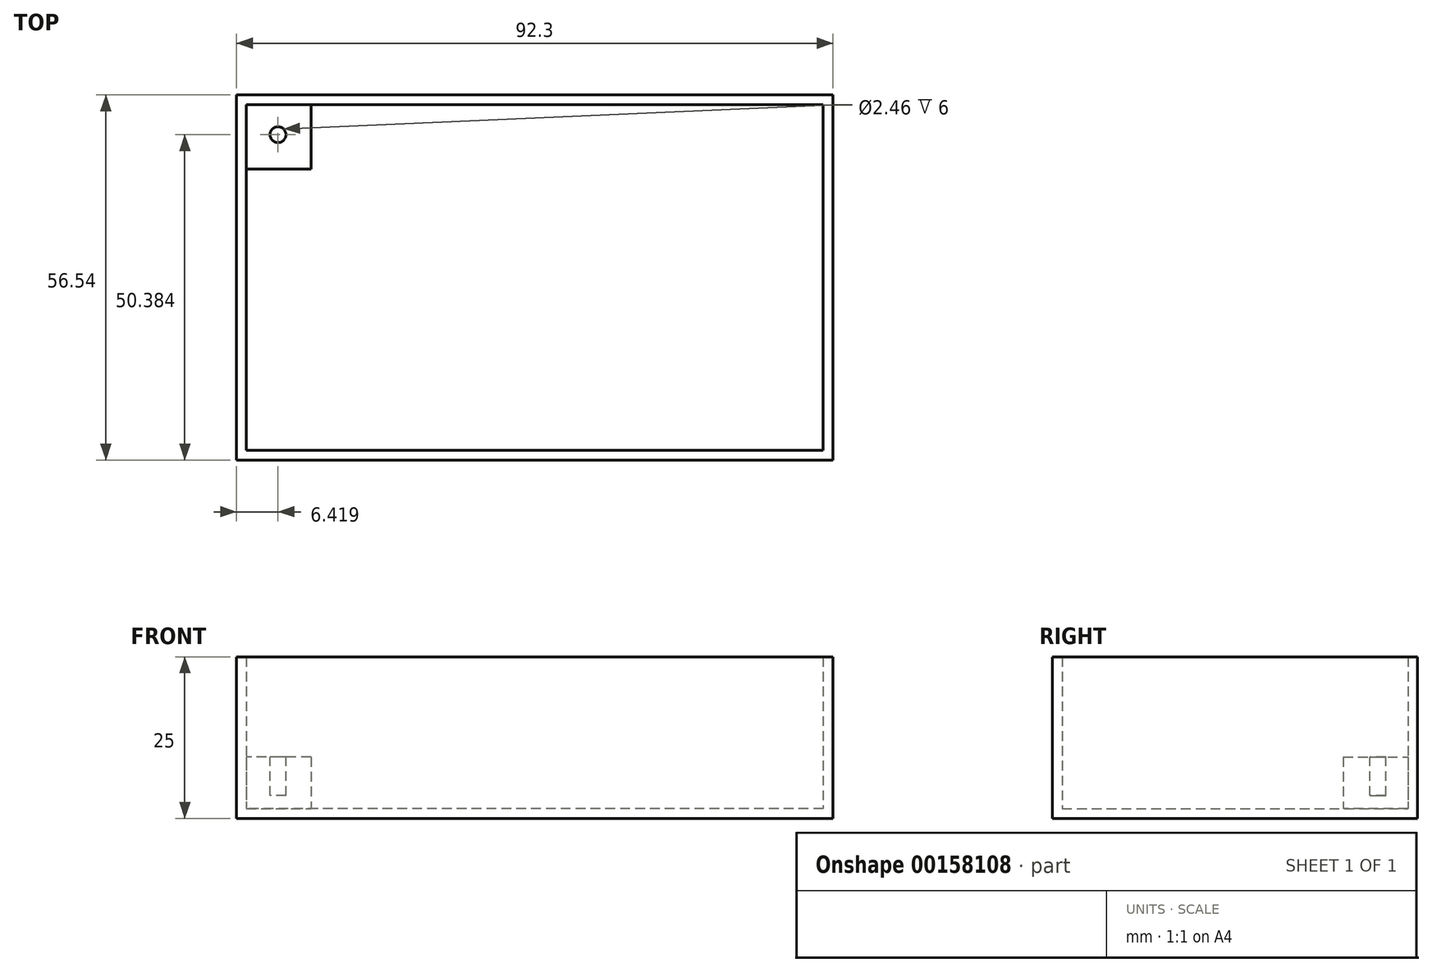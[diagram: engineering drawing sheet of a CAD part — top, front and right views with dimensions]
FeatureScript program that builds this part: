
annotation { "Feature Type Name" : "Feature", "Feature Type Description" : "" }
export const myFeature = defineFeature(function(context is Context, id is Id, definition is map)
    precondition{}
    {
        {
            var Q0;
            Q0=qCreatedBy(makeId("Top.planeOp"),FACE);
            var sketch = newSketch(context, id + "F0", { "sketchPlane" : qUnion([Q0])});
            skLineSegment(sketch, "E0.bottom", {"start": v(46.15, -28.27) * mm, "end": v(-46.15, -28.27) * mm});
            skLineSegment(sketch, "E0.top", {"start": v(46.15, 28.27) * mm, "end": v(-46.15, 28.27) * mm});
            skLineSegment(sketch, "E0.left", {"start": v(46.15, -28.27) * mm, "end": v(46.15, 28.27) * mm});
            skLineSegment(sketch, "E0.right", {"start": v(-46.15, -28.27) * mm, "end": v(-46.15, 28.27) * mm});
            skPoint(sketch, "E0.middle", {"position": v(0, 0) * mm});
            skSolve(sketch);
        }
        {
            var Q0;
            Q0=makeQuery(id+"F0.imprint","IMPRINT",FACE,{"disambiguationData":[TD([[makeQuery(id+"F0.imprint","IMPRINT",EDGE,{"derivedFrom":sQuery(id+"F0.wireOp",EDGE,"E0.bottom")}),-1.0]])]});
            extrude(context, id + "F1", {"entities" : qUnion([Q0]), "depth" : 25 * mm});
        }
        {
            var Q0;
            Q0=makeQuery(id+"F1.opExtrude","CAP_FACE",FACE,{"disambiguationData":[OSD([sQuery(id+"F0.wireOp",EDGE,"E0.bottom"),sQuery(id+"F0.wireOp",EDGE,"E0.top"),sQuery(id+"F0.wireOp",EDGE,"E0.left"),sQuery(id+"F0.wireOp",EDGE,"E0.right")])],"isStart":false});
            shell(context, id + "F2", {"entities" : qUnion([Q0]), "thickness" : 1.5 * mm});
        }
        {
            var Q0;
            Q0=makeQuery(id+"F2.opShell","OFFSET_FACE",FACE,{"disambiguationData":[OSD([sQuery(id+"F0.wireOp",EDGE,"E0.bottom"),sQuery(id+"F0.wireOp",EDGE,"E0.top"),sQuery(id+"F0.wireOp",EDGE,"E0.left"),sQuery(id+"F0.wireOp",EDGE,"E0.right")])]});
            var sketch = newSketch(context, id + "F3", { "sketchPlane" : qUnion([Q0])});
            skLineSegment(sketch, "E1.bottom", {"start": v(-44.65, 26.77) * mm, "end": v(-34.65, 26.77) * mm});
            skLineSegment(sketch, "E1.top", {"start": v(-44.65, 16.77) * mm, "end": v(-34.65, 16.77) * mm});
            skLineSegment(sketch, "E1.left", {"start": v(-44.65, 26.77) * mm, "end": v(-44.65, 16.77) * mm});
            skLineSegment(sketch, "E1.right", {"start": v(-34.65, 26.77) * mm, "end": v(-34.65, 16.77) * mm});
            skPoint(sketch, "E2", {"position": v(-39.86, 22.05) * mm});
            skPoint(sketch, "E3.MirrorP", {"position": v(-39.86, -22.05) * mm});
            skLineSegment(sketch, "E4.MirrorCS", {"start": v(-34.65, -26.77) * mm, "end": v(-34.65, -16.77) * mm});
            skLineSegment(sketch, "E5.MirrorCS", {"start": v(-44.65, -16.77) * mm, "end": v(-34.65, -16.77) * mm});
            skLineSegment(sketch, "E6.MirrorCS", {"start": v(34.65, 26.77) * mm, "end": v(34.65, 16.77) * mm});
            skLineSegment(sketch, "E7.MirrorCS", {"start": v(44.65, 16.77) * mm, "end": v(34.65, 16.77) * mm});
            skPoint(sketch, "E8.MirrorP", {"position": v(39.86, 22.05) * mm});
            skLineSegment(sketch, "E9.MirrorCS", {"start": v(44.65, -16.77) * mm, "end": v(34.65, -16.77) * mm});
            skLineSegment(sketch, "E10.MirrorCS", {"start": v(34.65, -26.77) * mm, "end": v(34.65, -16.77) * mm});
            skPoint(sketch, "E11.MirrorP", {"position": v(39.86, -22.05) * mm});
            skSolve(sketch);
        }
        {
            var Q0;
            Q0 = qSketchRegion(id + "F3", true);
            extrude(context, id + "F4", {"entities" : qUnion([Q0]), "operationType" : NewBodyOperationType.ADD, "depth" : 8 * mm});
        }
        {
            var Q0;
            Q0=makeQuery(id+"F4.opExtrude","CAP_FACE",FACE,{"disambiguationData":[OSD([sQuery(id+"F3.wireOp",EDGE,"E1.bottom"),sQuery(id+"F3.wireOp",EDGE,"E1.top"),sQuery(id+"F3.wireOp",EDGE,"E1.left"),sQuery(id+"F3.wireOp",EDGE,"E1.right")])],"isStart":false});
            var sketch = newSketch(context, id + "F5", { "sketchPlane" : qUnion([Q0])});
            skCircle(sketch, "E12", {"center": v(-39.73, 22.11) * mm, "radius": 1.23 * mm});
            skSolve(sketch);
        }
        {
            var Q0;
            Q0 = qSketchRegion(id + "F5", true);
            extrude(context, id + "F6", {"entities" : qUnion([Q0]), "operationType" : NewBodyOperationType.REMOVE, "oppositeDirection" : true, "depth" : 6 * mm});
        }
    });
